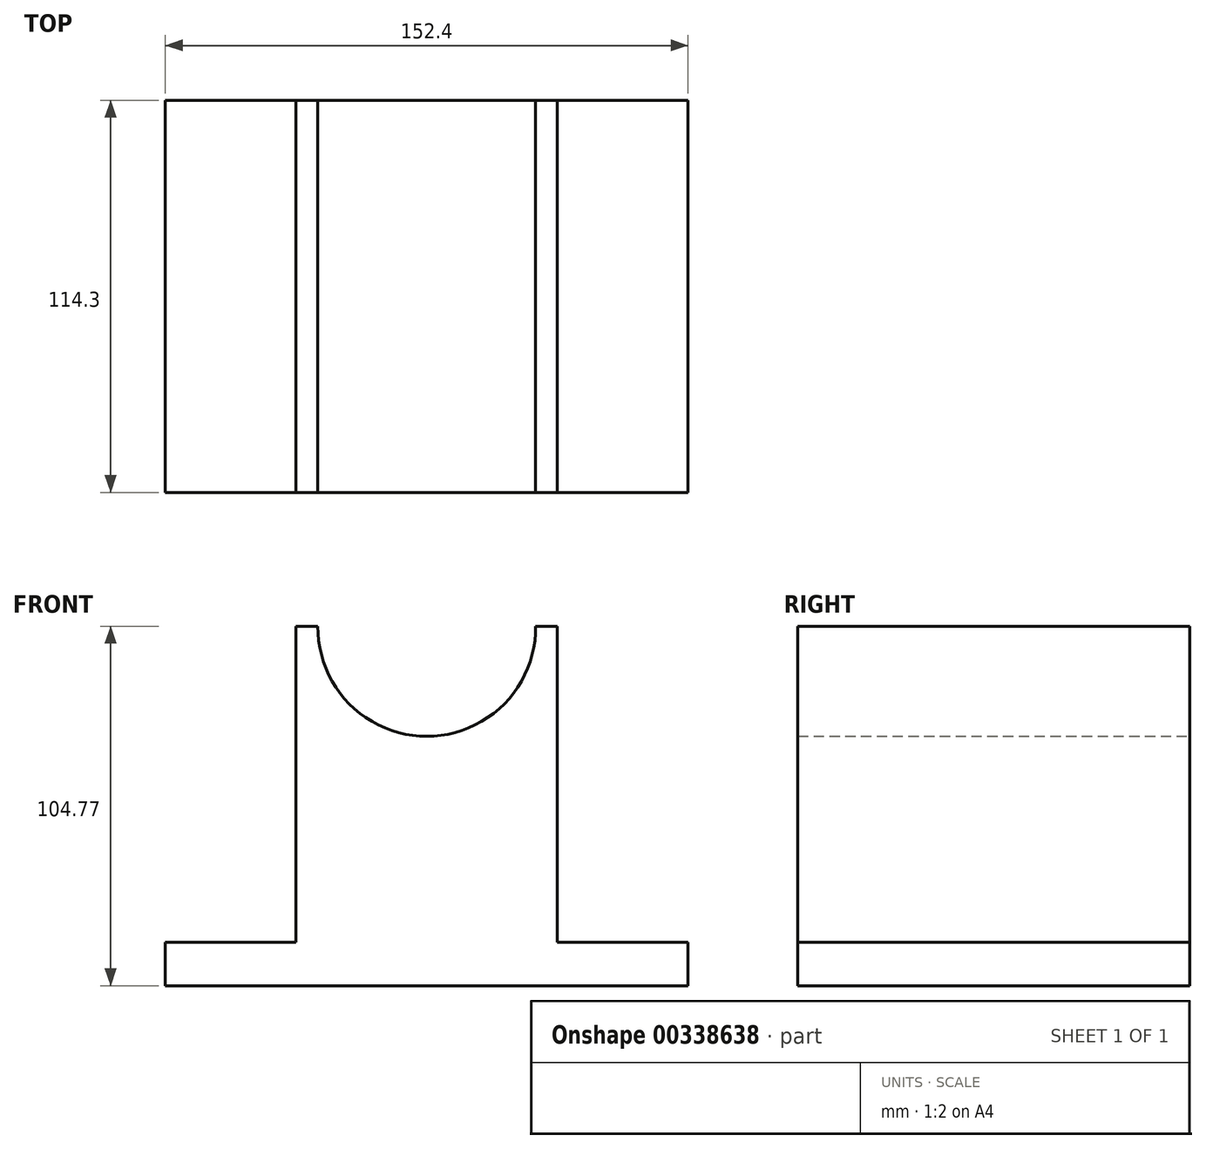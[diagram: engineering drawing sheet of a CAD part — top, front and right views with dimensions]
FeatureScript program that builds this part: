
annotation { "Feature Type Name" : "Feature", "Feature Type Description" : "" }
export const myFeature = defineFeature(function(context is Context, id is Id, definition is map)
    precondition{}
    {
        {
            var Q0;
            Q0=qCreatedBy(makeId("Front.planeOp"),FACE);
            var sketch = newSketch(context, id + "F0", { "sketchPlane" : qUnion([Q0])});
            skLineSegment(sketch, "E0", {"start": v(0, 0) * mm, "end": v(76.2, 0) * mm});
            skLineSegment(sketch, "E1", {"start": v(76.2, 0) * mm, "end": v(76.2, 12.7) * mm});
            skLineSegment(sketch, "E2", {"start": v(76.2, 12.7) * mm, "end": v(38.1, 12.7) * mm});
            skLineSegment(sketch, "E3", {"start": v(38.1, 12.7) * mm, "end": v(38.1, 104.78) * mm});
            skLineSegment(sketch, "E4", {"start": v(38.1, 104.78) * mm, "end": v(31.75, 104.78) * mm});
            skLineSegment(sketch, "E5.MirrorCS", {"start": v(-38.1, 12.7) * mm, "end": v(-38.1, 104.78) * mm});
            skLineSegment(sketch, "E6.MirrorCS", {"start": v(-38.1, 104.77) * mm, "end": v(-31.75, 104.77) * mm});
            skLineSegment(sketch, "E7.MirrorCS", {"start": v(-76.2, 12.7) * mm, "end": v(-38.1, 12.7) * mm});
            skLineSegment(sketch, "E8.MirrorCS", {"start": v(-76.2, 0) * mm, "end": v(-76.2, 12.7) * mm});
            skLineSegment(sketch, "E9", {"start": v(-76.2, 0) * mm, "end": v(0, 0) * mm});
            skArc(sketch, "E10", {"start": v(-31.75, 104.77) * mm, "mid": v(0, 72.67) * mm, "end": v(31.75, 104.77) * mm});
            skSolve(sketch);
        }
        {
            var Q0;
            Q0 = qSketchRegion(id + "F0", true);
            extrude(context, id + "F1", {"entities" : qUnion([Q0]), "depth" : 114.3 * mm});
        }
    });
